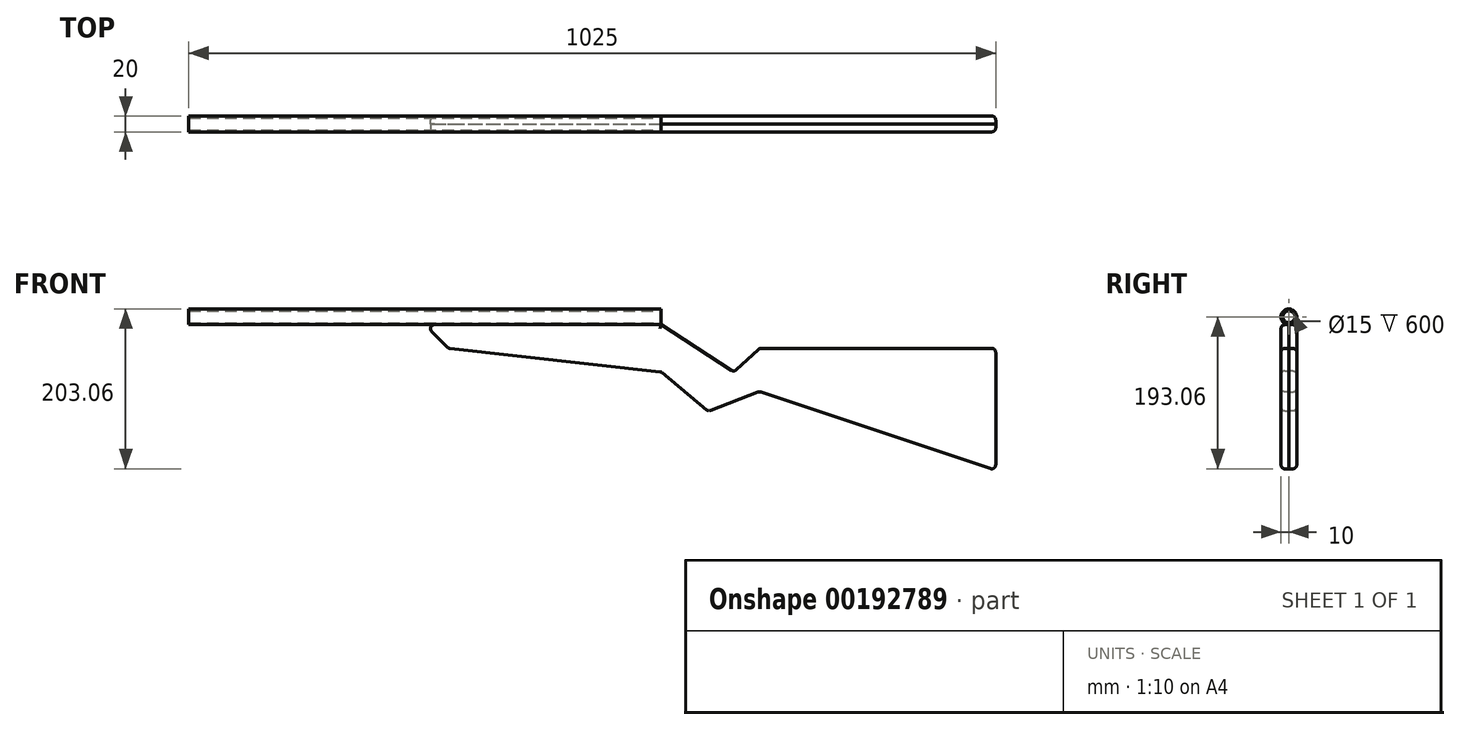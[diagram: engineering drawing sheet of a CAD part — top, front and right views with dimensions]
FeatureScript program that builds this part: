
annotation { "Feature Type Name" : "Feature", "Feature Type Description" : "" }
export const myFeature = defineFeature(function(context is Context, id is Id, definition is map)
    precondition{}
    {
        {
            var Q0;
            Q0=qCreatedBy(makeId("Right.planeOp"),FACE);
            var sketch = newSketch(context, id + "F0", { "sketchPlane" : qUnion([Q0])});
            skCircle(sketch, "E0", {"center": v(0, 0) * mm, "radius": 10 * mm});
            skSolve(sketch);
        }
        {
            var Q0;
            Q0 = qSketchRegion(id + "F0", true);
            extrude(context, id + "F1", {"entities" : qUnion([Q0]), "depth" : 300 * mm});
        }
        {
            var Q0;
            Q0=makeQuery(id+"F1.opExtrude","CAP_FACE",FACE,{"disambiguationData":[OSD([sQuery(id+"F0.wireOp",EDGE,"E0")])],"isStart":false});
            var sketch = newSketch(context, id + "F2", { "sketchPlane" : qUnion([Q0])});
            skCircle(sketch, "E1", {"center": v(0, 0) * mm, "radius": 7.5 * mm});
            skSolve(sketch);
        }
        {
            var Q0;
            Q0 = qSketchRegion(id + "F2", true);
            extrude(context, id + "F3", {"entities" : qUnion([Q0]), "operationType" : NewBodyOperationType.REMOVE, "oppositeDirection" : true, "depth" : 300 * mm});
        }
        {
            var Q0;
            Q0=makeQuery(id+"F1.opExtrude","SWEPT_BODY",BODY,{"disambiguationData":[OSD([sQuery(id+"F0.wireOp",EDGE,"E0")])]});
            var Q1;
            Q1=qCreatedBy(makeId("Right.planeOp"),FACE);
            mirror(context, id + "F4", {"operationType" : NewBodyOperationType.ADD, "entities" : qUnion([Q0]), "mirrorPlane" : qUnion([Q1])});
        }
        {
            var Q0;
            Q0=qCreatedBy(makeId("Front.planeOp"),FACE);
            var sketch = newSketch(context, id + "F5", { "sketchPlane" : qUnion([Q0])});
            skLineSegment(sketch, "E2", {"start": v(0, 0) * mm, "end": v(0, -10) * mm, "construction": true});
            skLineSegment(sketch, "E3", {"start": v(0, -10) * mm, "end": v(300, -10) * mm, "construction": true});
            skLineSegment(sketch, "E4", {"start": v(0, -10) * mm, "end": v(0, -40) * mm, "construction": true});
            skLineSegment(sketch, "E5", {"start": v(0, -40) * mm, "end": v(30, -40) * mm, "construction": true});
            skLineSegment(sketch, "E6", {"start": v(0, -10) * mm, "end": v(30, -40) * mm});
            skLineSegment(sketch, "E7", {"start": v(30, -40) * mm, "end": v(30, -70) * mm, "construction": true});
            skLineSegment(sketch, "E8", {"start": v(30, -70) * mm, "end": v(300, -70) * mm, "construction": true});
            skLineSegment(sketch, "E9", {"start": v(30, -40) * mm, "end": v(300, -70) * mm});
            skLineSegment(sketch, "E10", {"start": v(300, -70) * mm, "end": v(360, -70) * mm, "construction": true});
            skLineSegment(sketch, "E11", {"start": v(360, -70) * mm, "end": v(360, -120) * mm, "construction": true});
            skLineSegment(sketch, "E12", {"start": v(360, -120) * mm, "end": v(425, -120) * mm, "construction": true});
            skLineSegment(sketch, "E13", {"start": v(300, -70) * mm, "end": v(360, -120) * mm});
            skLineSegment(sketch, "E14", {"start": v(425, -120) * mm, "end": v(425, -95) * mm, "construction": true});
            skLineSegment(sketch, "E15", {"start": v(425, -95) * mm, "end": v(725, -95) * mm, "construction": true});
            skLineSegment(sketch, "E16", {"start": v(725, -95) * mm, "end": v(725, -195) * mm, "construction": true});
            skLineSegment(sketch, "E17", {"start": v(360, -120) * mm, "end": v(425, -95) * mm});
            skLineSegment(sketch, "E18", {"start": v(425, -95) * mm, "end": v(725, -195) * mm});
            skLineSegment(sketch, "E19", {"start": v(725, -95) * mm, "end": v(725, -195) * mm});
            skLineSegment(sketch, "E20", {"start": v(725, -95) * mm, "end": v(725, -40) * mm, "construction": true});
            skLineSegment(sketch, "E21", {"start": v(725, -40) * mm, "end": v(425, -40) * mm, "construction": true});
            skLineSegment(sketch, "E22", {"start": v(425, -40) * mm, "end": v(425, -70) * mm, "construction": true});
            skLineSegment(sketch, "E23", {"start": v(425, -70) * mm, "end": v(392.5, -70) * mm, "construction": true});
            skPoint(sketch, "E23.endSnap0", {"position": v(392.5, -120) * mm});
            skLineSegment(sketch, "E24", {"start": v(392.5, -70) * mm, "end": v(392.5, -10) * mm, "construction": true});
            skLineSegment(sketch, "E25", {"start": v(392.5, -10) * mm, "end": v(300, -10) * mm, "construction": true});
            skLineSegment(sketch, "E26", {"start": v(725, -95) * mm, "end": v(725, -40) * mm});
            skLineSegment(sketch, "E27", {"start": v(425, -40) * mm, "end": v(725, -40) * mm});
            skLineSegment(sketch, "E28", {"start": v(425, -40) * mm, "end": v(392.5, -70) * mm});
            skLineSegment(sketch, "E29", {"start": v(300, -10) * mm, "end": v(392.5, -70) * mm});
            skLineSegment(sketch, "E30", {"start": v(0, -10) * mm, "end": v(300, -10) * mm});
            skSolve(sketch);
        }
        {
            var Q0;
            Q0 = qSketchRegion(id + "F5", true);
            extrude(context, id + "F6", {"entities" : qUnion([Q0]), "depth" : 10 * mm});
        }
        {
            var Q0;
            Q0=makeQuery(id+"F6.opExtrude","SWEPT_BODY",BODY,{"disambiguationData":[OSD([sQuery(id+"F5.wireOp",EDGE,"E6"),sQuery(id+"F5.wireOp",EDGE,"E9"),sQuery(id+"F5.wireOp",EDGE,"E13"),sQuery(id+"F5.wireOp",EDGE,"E17"),sQuery(id+"F5.wireOp",EDGE,"E18"),sQuery(id+"F5.wireOp",EDGE,"E19"),sQuery(id+"F5.wireOp",EDGE,"E26"),sQuery(id+"F5.wireOp",EDGE,"E27"),sQuery(id+"F5.wireOp",EDGE,"E28"),sQuery(id+"F5.wireOp",EDGE,"E29"),sQuery(id+"F5.wireOp",EDGE,"E30")])]});
            var Q1;
            Q1=makeQuery(id+"F6.opExtrude","CAP_FACE",FACE,{"disambiguationData":[OSD([sQuery(id+"F5.wireOp",EDGE,"E6"),sQuery(id+"F5.wireOp",EDGE,"E9"),sQuery(id+"F5.wireOp",EDGE,"E13"),sQuery(id+"F5.wireOp",EDGE,"E17"),sQuery(id+"F5.wireOp",EDGE,"E18"),sQuery(id+"F5.wireOp",EDGE,"E19"),sQuery(id+"F5.wireOp",EDGE,"E26"),sQuery(id+"F5.wireOp",EDGE,"E27"),sQuery(id+"F5.wireOp",EDGE,"E28"),sQuery(id+"F5.wireOp",EDGE,"E29"),sQuery(id+"F5.wireOp",EDGE,"E30")])],"isStart":true});
            mirror(context, id + "F7", {"operationType" : NewBodyOperationType.ADD, "entities" : qUnion([Q0]), "mirrorPlane" : qUnion([Q1])});
        }
        {
            var Q0;
            Q0=makeQuery(id+"F6.opExtrude","CAP_EDGE",EDGE,{"disambiguationData":[OSD([sQuery(id+"F5.wireOp",EDGE,"E6")])],"isStart":false});
            var Q1;
            Q1=makeQuery(id+"F7.opPattern","COPY",EDGE,{"derivedFrom":makeQuery(id+"F6.opExtrude","CAP_EDGE",EDGE,{"disambiguationData":[OSD([sQuery(id+"F5.wireOp",EDGE,"E6")])],"isStart":false}),"instanceName":"1"});
            var Q2;
            Q2=makeQuery(id+"F7.opPattern","COPY",EDGE,{"derivedFrom":makeQuery(id+"F6.opExtrude","CAP_EDGE",EDGE,{"disambiguationData":[OSD([sQuery(id+"F5.wireOp",EDGE,"E9")])],"isStart":false}),"instanceName":"1"});
            var Q3;
            Q3=makeQuery(id+"F6.opExtrude","CAP_EDGE",EDGE,{"disambiguationData":[OSD([sQuery(id+"F5.wireOp",EDGE,"E9")])],"isStart":false});
            var Q4;
            {var subQ0=makeQuery(id+"F6.opExtrude","SWEPT_EDGE",EDGE,{"disambiguationData":[OSD([sQuery(id+"F5.wireOp",EDGE,"E6"),sQuery(id+"F5.wireOp",EDGE,"E9")])]});Q4=makeQuery(id+"F7.boolean.opBoolean","MERGE",EDGE,{"derivedFrom":[subQ0,makeQuery(id+"F7.opPattern","COPY",EDGE,{"derivedFrom":subQ0,"instanceName":"1"})]});}
            var Q5;
            Q5=makeQuery(id+"F6.opExtrude","CAP_EDGE",EDGE,{"disambiguationData":[OSD([sQuery(id+"F5.wireOp",EDGE,"E13")])],"isStart":false});
            var Q6;
            Q6=makeQuery(id+"F7.opPattern","COPY",EDGE,{"derivedFrom":makeQuery(id+"F6.opExtrude","CAP_EDGE",EDGE,{"disambiguationData":[OSD([sQuery(id+"F5.wireOp",EDGE,"E13")])],"isStart":false}),"instanceName":"1"});
            var Q7;
            Q7=makeQuery(id+"F6.opExtrude","CAP_EDGE",EDGE,{"disambiguationData":[OSD([sQuery(id+"F5.wireOp",EDGE,"E17")])],"isStart":false});
            var Q8;
            Q8=makeQuery(id+"F7.opPattern","COPY",EDGE,{"derivedFrom":makeQuery(id+"F6.opExtrude","CAP_EDGE",EDGE,{"disambiguationData":[OSD([sQuery(id+"F5.wireOp",EDGE,"E17")])],"isStart":false}),"instanceName":"1"});
            var Q9;
            Q9=makeQuery(id+"F7.opPattern","COPY",EDGE,{"derivedFrom":makeQuery(id+"F6.opExtrude","CAP_EDGE",EDGE,{"disambiguationData":[OSD([sQuery(id+"F5.wireOp",EDGE,"E18")])],"isStart":false}),"instanceName":"1"});
            var Q10;
            Q10=makeQuery(id+"F6.opExtrude","CAP_EDGE",EDGE,{"disambiguationData":[OSD([sQuery(id+"F5.wireOp",EDGE,"E18")])],"isStart":false});
            var Q11;
            Q11=makeQuery(id+"F6.opExtrude","CAP_EDGE",EDGE,{"disambiguationData":[OSD([sQuery(id+"F5.wireOp",EDGE,"E19"),sQuery(id+"F5.wireOp",EDGE,"E26")])],"isStart":false});
            var Q12;
            Q12=makeQuery(id+"F6.opExtrude","CAP_EDGE",EDGE,{"disambiguationData":[OSD([sQuery(id+"F5.wireOp",EDGE,"E27")])],"isStart":false});
            var Q13;
            Q13=makeQuery(id+"F6.opExtrude","CAP_EDGE",EDGE,{"disambiguationData":[OSD([sQuery(id+"F5.wireOp",EDGE,"E28")])],"isStart":false});
            var Q14;
            Q14=makeQuery(id+"F6.opExtrude","CAP_EDGE",EDGE,{"disambiguationData":[OSD([sQuery(id+"F5.wireOp",EDGE,"E29")])],"isStart":false});
            var Q15;
            Q15=makeQuery(id+"F6.opExtrude","CAP_EDGE",EDGE,{"disambiguationData":[OSD([sQuery(id+"F5.wireOp",EDGE,"E30")])],"isStart":false});
            var Q16;
            Q16=makeQuery(id+"F7.opPattern","COPY",EDGE,{"derivedFrom":makeQuery(id+"F6.opExtrude","CAP_EDGE",EDGE,{"disambiguationData":[OSD([sQuery(id+"F5.wireOp",EDGE,"E30")])],"isStart":false}),"instanceName":"1"});
            var Q17;
            Q17=makeQuery(id+"F7.opPattern","COPY",EDGE,{"derivedFrom":makeQuery(id+"F6.opExtrude","CAP_EDGE",EDGE,{"disambiguationData":[OSD([sQuery(id+"F5.wireOp",EDGE,"E29")])],"isStart":false}),"instanceName":"1"});
            var Q18;
            Q18=makeQuery(id+"F7.opPattern","COPY",EDGE,{"derivedFrom":makeQuery(id+"F6.opExtrude","CAP_EDGE",EDGE,{"disambiguationData":[OSD([sQuery(id+"F5.wireOp",EDGE,"E27")])],"isStart":false}),"instanceName":"1"});
            var Q19;
            Q19=makeQuery(id+"F7.opPattern","COPY",EDGE,{"derivedFrom":makeQuery(id+"F6.opExtrude","CAP_EDGE",EDGE,{"disambiguationData":[OSD([sQuery(id+"F5.wireOp",EDGE,"E28")])],"isStart":false}),"instanceName":"1"});
            var Q20;
            {var subQ0=makeQuery(id+"F6.opExtrude","SWEPT_EDGE",EDGE,{"disambiguationData":[OSD([sQuery(id+"F5.wireOp",EDGE,"E28"),sQuery(id+"F5.wireOp",EDGE,"E29")])]});Q20=makeQuery(id+"F7.boolean.opBoolean","MERGE",EDGE,{"derivedFrom":[subQ0,makeQuery(id+"F7.opPattern","COPY",EDGE,{"derivedFrom":subQ0,"instanceName":"1"})]});}
            var Q21;
            {var subQ0=makeQuery(id+"F6.opExtrude","SWEPT_EDGE",EDGE,{"disambiguationData":[OSD([sQuery(id+"F5.wireOp",EDGE,"E27"),sQuery(id+"F5.wireOp",EDGE,"E28")])]});Q21=makeQuery(id+"F7.boolean.opBoolean","MERGE",EDGE,{"derivedFrom":[subQ0,makeQuery(id+"F7.opPattern","COPY",EDGE,{"derivedFrom":subQ0,"instanceName":"1"})]});}
            var Q22;
            Q22=makeQuery(id+"F7.opPattern","COPY",EDGE,{"derivedFrom":makeQuery(id+"F6.opExtrude","CAP_EDGE",EDGE,{"disambiguationData":[OSD([sQuery(id+"F5.wireOp",EDGE,"E19"),sQuery(id+"F5.wireOp",EDGE,"E26")])],"isStart":false}),"instanceName":"1"});
            var Q23;
            {var subQ0=makeQuery(id+"F6.opExtrude","SWEPT_EDGE",EDGE,{"disambiguationData":[OSD([sQuery(id+"F5.wireOp",EDGE,"E26"),sQuery(id+"F5.wireOp",EDGE,"E27")])]});Q23=makeQuery(id+"F7.boolean.opBoolean","MERGE",EDGE,{"derivedFrom":[subQ0,makeQuery(id+"F7.opPattern","COPY",EDGE,{"derivedFrom":subQ0,"instanceName":"1"})]});}
            var Q24;
            {var subQ0=makeQuery(id+"F6.opExtrude","SWEPT_EDGE",EDGE,{"disambiguationData":[OSD([sQuery(id+"F5.wireOp",EDGE,"E18"),sQuery(id+"F5.wireOp",EDGE,"E19")])]});Q24=makeQuery(id+"F7.boolean.opBoolean","MERGE",EDGE,{"derivedFrom":[subQ0,makeQuery(id+"F7.opPattern","COPY",EDGE,{"derivedFrom":subQ0,"instanceName":"1"})]});}
            var Q25;
            {var subQ0=makeQuery(id+"F6.opExtrude","SWEPT_EDGE",EDGE,{"disambiguationData":[OSD([sQuery(id+"F5.wireOp",EDGE,"E17"),sQuery(id+"F5.wireOp",EDGE,"E18")])]});Q25=makeQuery(id+"F7.boolean.opBoolean","MERGE",EDGE,{"derivedFrom":[subQ0,makeQuery(id+"F7.opPattern","COPY",EDGE,{"derivedFrom":subQ0,"instanceName":"1"})]});}
            var Q26;
            {var subQ0=makeQuery(id+"F6.opExtrude","SWEPT_EDGE",EDGE,{"disambiguationData":[OSD([sQuery(id+"F5.wireOp",EDGE,"E13"),sQuery(id+"F5.wireOp",EDGE,"E17")])]});Q26=makeQuery(id+"F7.boolean.opBoolean","MERGE",EDGE,{"derivedFrom":[subQ0,makeQuery(id+"F7.opPattern","COPY",EDGE,{"derivedFrom":subQ0,"instanceName":"1"})]});}
            var Q27;
            {var subQ0=makeQuery(id+"F6.opExtrude","SWEPT_EDGE",EDGE,{"disambiguationData":[OSD([sQuery(id+"F5.wireOp",EDGE,"E9"),sQuery(id+"F5.wireOp",EDGE,"E13")])]});Q27=makeQuery(id+"F7.boolean.opBoolean","MERGE",EDGE,{"derivedFrom":[subQ0,makeQuery(id+"F7.opPattern","COPY",EDGE,{"derivedFrom":subQ0,"instanceName":"1"})]});}
            var Q28;
            {var subQ0=makeQuery(id+"F6.opExtrude","SWEPT_EDGE",EDGE,{"disambiguationData":[OSD([sQuery(id+"F5.wireOp",EDGE,"E6"),sQuery(id+"F5.wireOp",EDGE,"E30")])]});Q28=makeQuery(id+"F7.boolean.opBoolean","MERGE",EDGE,{"derivedFrom":[subQ0,makeQuery(id+"F7.opPattern","COPY",EDGE,{"derivedFrom":subQ0,"instanceName":"1"})]});}
            fillet(context, id + "F8", {"entities" : qUnion([Q0, Q1, Q2, Q3, Q4, Q5, Q6, Q7, Q8, Q9, Q10, Q11, Q12, Q13, Q14, Q15, Q16, Q17, Q18, Q19, Q20, Q21, Q22, Q23, Q24, Q25, Q26, Q27, Q28]), "radius" : 5 * mm, "tangentPropagation" : true, "allowEdgeOverflow" : false});
        }
    });
